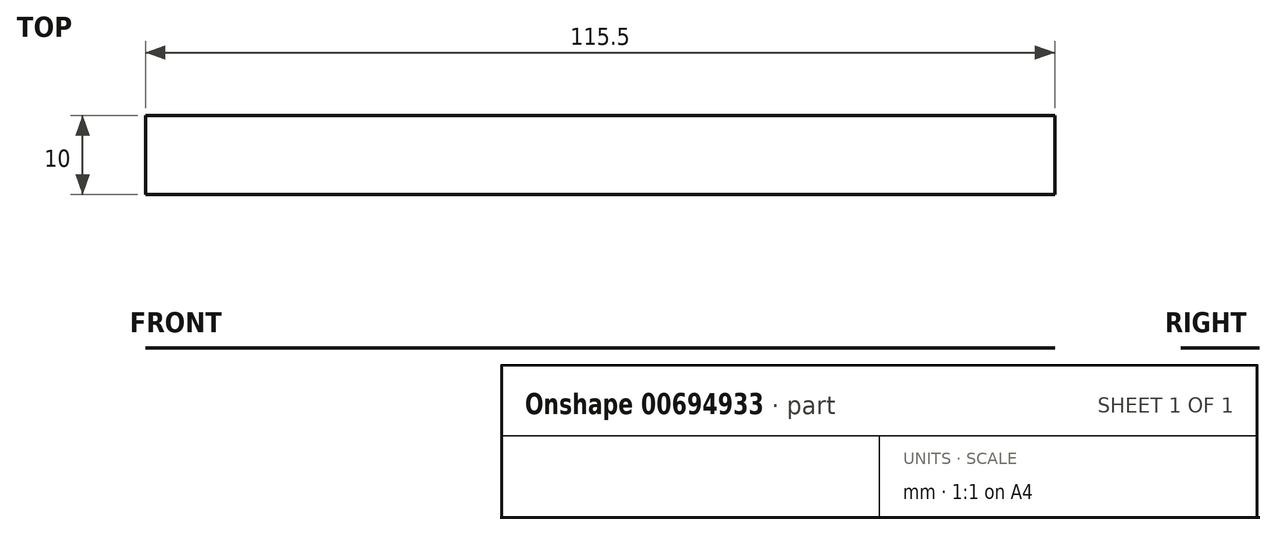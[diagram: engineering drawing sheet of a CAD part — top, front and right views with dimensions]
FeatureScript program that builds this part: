
annotation { "Feature Type Name" : "Feature", "Feature Type Description" : "" }
export const myFeature = defineFeature(function(context is Context, id is Id, definition is map)
    precondition{}
    {
        {
            var Q0;
            Q0=qCreatedBy(makeId("Front.planeOp"),FACE);
            var sketch = newSketch(context, id + "F0", { "sketchPlane" : qUnion([Q0])});
            skLineSegment(sketch, "E0.bottom", {"start": v(57.75, 17.4) * mm, "end": v(-57.75, 17.4) * mm});
            skLineSegment(sketch, "E0.top", {"start": v(57.75, -17.4) * mm, "end": v(-57.75, -17.4) * mm});
            skLineSegment(sketch, "E0.left", {"start": v(57.75, 17.4) * mm, "end": v(57.75, -17.4) * mm});
            skLineSegment(sketch, "E0.right", {"start": v(-57.75, 17.4) * mm, "end": v(-57.75, -17.4) * mm});
            skPoint(sketch, "E0.middle", {"position": v(0, 0) * mm});
            skSolve(sketch);
        }
        {
            var Q0;
            Q0=sQuery(id+"F0.wireOp",EDGE,"E0.bottom");
            extrude(context, id + "F1", {"bodyType" : ToolBodyType.SURFACE, "surfaceEntities" : qUnion([Q0]), "depth" : 10 * mm, "offsetDistance" : 25 * mm});
        }
    });
